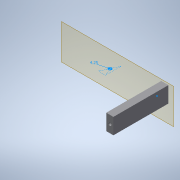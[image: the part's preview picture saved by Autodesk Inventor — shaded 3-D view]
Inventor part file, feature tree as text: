
AUTODESK INVENTOR PART (.ipt)
format: ipt  version: 2020 (Build 240168000, 168)  size: 122,368 bytes
history: native  units: mm
features: other x6, extrude x3, sketch x3, reference x2
ambient origin geometry x8: Origin, YZ Plane, XZ Plane, XY Plane, X Axis, Y Axis, Z Axis, Center Point
bodies: Body1 (feature_tree)
feature tree (14):
  other  "Bryła1"
  other  "Płaszczyzna konstrukcyjna1"
  extrude  "Wyciągnięcie proste1"  Depth=76.0mm TaperAngle=0.0deg
  sketch  "Szkic2"
  extrude  "Wyciągnięcie proste3"  Depth=10.0mm
  extrude  "Wyciągnięcie proste2"  Depth=10.0mm
  sketch  "Szkic1"
  reference  "Odniesienie1"
  reference  "Odniesienie2"
  sketch  "Szkic3"
  other  "<userpath>\Desktop\3d\scanning-robot\Assembly1.iam"
  other  "Assembly1.iam"
  other  "base:1"
  other  "wheel-adapter:1"
